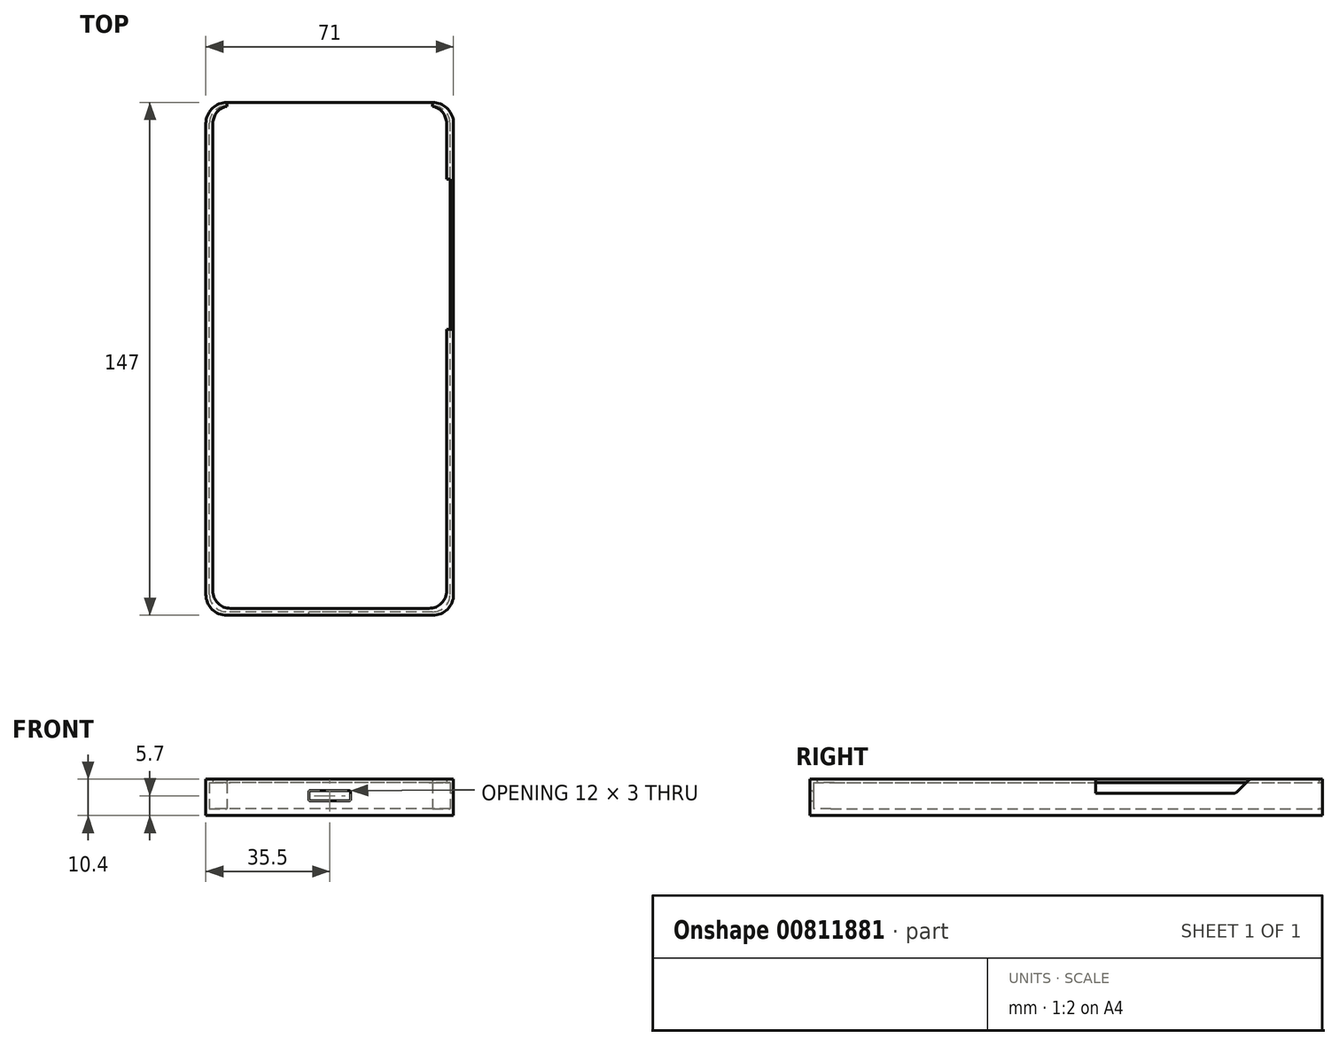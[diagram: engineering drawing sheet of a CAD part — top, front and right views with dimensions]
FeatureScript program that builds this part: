
annotation { "Feature Type Name" : "Feature", "Feature Type Description" : "" }
export const myFeature = defineFeature(function(context is Context, id is Id, definition is map)
    precondition{}
    {
        {
            var Q0;
            Q0=qCreatedBy(makeId("Top.planeOp"),FACE);
            var sketch = newSketch(context, id + "F0", { "sketchPlane" : qUnion([Q0])});
            skLineSegment(sketch, "E0.bottom", {"start": v(29.5, -72.5) * mm, "end": v(-29.5, -72.5) * mm});
            skLineSegment(sketch, "E0.top", {"start": v(29.5, 72.5) * mm, "end": v(-29.5, 72.5) * mm});
            skLineSegment(sketch, "E0.left", {"start": v(34.5, -67.5) * mm, "end": v(34.5, 67.5) * mm});
            skLineSegment(sketch, "E0.right", {"start": v(-34.5, -67.5) * mm, "end": v(-34.5, 67.5) * mm});
            skPoint(sketch, "E0.middle", {"position": v(0, 0) * mm});
            skLineSegment(sketch, "E1.bottom", {"start": v(29.5, -73.5) * mm, "end": v(-29.5, -73.5) * mm});
            skLineSegment(sketch, "E1.top", {"start": v(29.5, 73.5) * mm, "end": v(-29.5, 73.5) * mm});
            skLineSegment(sketch, "E1.left", {"start": v(35.5, -67.5) * mm, "end": v(35.5, 67.5) * mm});
            skLineSegment(sketch, "E1.right", {"start": v(-35.5, -67.5) * mm, "end": v(-35.5, 67.5) * mm});
            skPoint(sketch, "E2.visualSharp", {"position": v(-34.5, 72.5) * mm});
            skArc(sketch, "E2.filletArc", {"start": v(-29.5, 72.5) * mm, "mid": v(-33.04, 71.04) * mm, "end": v(-34.5, 67.5) * mm});
            skPoint(sketch, "E3.visualSharp", {"position": v(-34.5, -72.5) * mm});
            skArc(sketch, "E3.filletArc", {"start": v(-34.5, -67.5) * mm, "mid": v(-33.04, -71.04) * mm, "end": v(-29.5, -72.5) * mm});
            skPoint(sketch, "E4.visualSharp", {"position": v(34.5, -72.5) * mm});
            skArc(sketch, "E4.filletArc", {"start": v(29.5, -72.5) * mm, "mid": v(33.04, -71.04) * mm, "end": v(34.5, -67.5) * mm});
            skPoint(sketch, "E5.visualSharp", {"position": v(34.5, 72.5) * mm});
            skArc(sketch, "E5.filletArc", {"start": v(34.5, 67.5) * mm, "mid": v(33.04, 71.04) * mm, "end": v(29.5, 72.5) * mm});
            skPoint(sketch, "E6.visualSharp", {"position": v(-35.5, 73.5) * mm});
            skArc(sketch, "E6.filletArc", {"start": v(-29.5, 73.5) * mm, "mid": v(-33.74, 71.74) * mm, "end": v(-35.5, 67.5) * mm});
            skPoint(sketch, "E7.visualSharp", {"position": v(-35.5, -73.5) * mm});
            skArc(sketch, "E7.filletArc", {"start": v(-35.5, -67.5) * mm, "mid": v(-33.74, -71.74) * mm, "end": v(-29.5, -73.5) * mm});
            skPoint(sketch, "E8.visualSharp", {"position": v(35.5, -73.5) * mm});
            skArc(sketch, "E8.filletArc", {"start": v(29.5, -73.5) * mm, "mid": v(33.74, -71.74) * mm, "end": v(35.5, -67.5) * mm});
            skPoint(sketch, "E9.visualSharp", {"position": v(35.5, 73.5) * mm});
            skArc(sketch, "E9.filletArc", {"start": v(35.5, 67.5) * mm, "mid": v(33.74, 71.74) * mm, "end": v(29.5, 73.5) * mm});
            skSolve(sketch);
        }
        {
            var Q0;
            Q0=makeQuery(id+"F0.imprint","IMPRINT",FACE,{"disambiguationData":[TD([[makeQuery(id+"F0.imprint","IMPRINT",EDGE,{"derivedFrom":sQuery(id+"F0.wireOp",EDGE,"E0.bottom")}),-1.0]])]});
            extrude(context, id + "F1", {"entities" : qUnion([Q0]), "depth" : 1 * mm});
        }
        {
            var Q0;
            Q0=makeQuery(id+"F0.imprint","IMPRINT",FACE,{"disambiguationData":[TD([[makeQuery(id+"F0.imprint","IMPRINT",EDGE,{"derivedFrom":sQuery(id+"F0.wireOp",EDGE,"E0.bottom")}),1.0]])]});
            extrude(context, id + "F2", {"entities" : qUnion([Q0]), "operationType" : NewBodyOperationType.ADD, "depth" : (1 + 7.4) * mm});
        }
        {
            var Q0;
            Q0=makeQuery(id+"F2.opExtrude","CAP_FACE",FACE,{"disambiguationData":[OSD([sQuery(id+"F0.wireOp",EDGE,"E0.bottom"),sQuery(id+"F0.wireOp",EDGE,"E0.top"),sQuery(id+"F0.wireOp",EDGE,"E0.left"),sQuery(id+"F0.wireOp",EDGE,"E0.right"),sQuery(id+"F0.wireOp",EDGE,"E1.bottom"),sQuery(id+"F0.wireOp",EDGE,"E1.top"),sQuery(id+"F0.wireOp",EDGE,"E1.left"),sQuery(id+"F0.wireOp",EDGE,"E1.right"),sQuery(id+"F0.wireOp",EDGE,"E2.filletArc"),sQuery(id+"F0.wireOp",EDGE,"E3.filletArc"),sQuery(id+"F0.wireOp",EDGE,"E4.filletArc"),sQuery(id+"F0.wireOp",EDGE,"E5.filletArc"),sQuery(id+"F0.wireOp",EDGE,"E6.filletArc"),sQuery(id+"F0.wireOp",EDGE,"E7.filletArc"),sQuery(id+"F0.wireOp",EDGE,"E8.filletArc"),sQuery(id+"F0.wireOp",EDGE,"E9.filletArc")])],"isStart":false});
            var sketch = newSketch(context, id + "F3", { "sketchPlane" : qUnion([Q0])});
            skLineSegment(sketch, "E10.bottom", {"start": v(28.5, -71.5) * mm, "end": v(-28.5, -71.5) * mm});
            skLineSegment(sketch, "E10.top", {"start": v(28.5, 72.5) * mm, "end": v(-28.5, 72.5) * mm});
            skLineSegment(sketch, "E10.left", {"start": v(33.5, -66.5) * mm, "end": v(33.5, 67.5) * mm});
            skLineSegment(sketch, "E10.right", {"start": v(-33.5, -66.5) * mm, "end": v(-33.5, 67.5) * mm});
            skPoint(sketch, "E10.middle", {"position": v(0, 0.5) * mm});
            skPoint(sketch, "E11.visualSharp", {"position": v(-33.5, -71.5) * mm});
            skArc(sketch, "E11.filletArc", {"start": v(-33.5, -66.5) * mm, "mid": v(-32.04, -70.04) * mm, "end": v(-28.5, -71.5) * mm});
            skPoint(sketch, "E12.visualSharp", {"position": v(33.5, -71.5) * mm});
            skArc(sketch, "E12.filletArc", {"start": v(28.5, -71.5) * mm, "mid": v(32.04, -70.04) * mm, "end": v(33.5, -66.5) * mm});
            skPoint(sketch, "E13.visualSharp", {"position": v(33.5, 72.5) * mm});
            skArc(sketch, "E13.filletArc", {"start": v(33.5, 67.5) * mm, "mid": v(32.04, 71.04) * mm, "end": v(28.5, 72.5) * mm});
            skPoint(sketch, "E14.visualSharp", {"position": v(-33.5, 72.5) * mm});
            skArc(sketch, "E14.filletArc", {"start": v(-28.5, 72.5) * mm, "mid": v(-32.04, 71.04) * mm, "end": v(-33.5, 67.5) * mm});
            skSolve(sketch);
        }
        {
            var Q0;
            Q0=makeQuery(id+"F3.imprint","IMPRINT",FACE,{"disambiguationData":[TD([[makeQuery(id+"F3.imprint","IMPRINT",EDGE,{"derivedFrom":sQuery(id+"F3.wireOp",EDGE,"E10.bottom")}),1.0]])]});
            var Q1;
            Q1=makeQuery(id+"F3.imprint","IMPRINT",FACE,{"disambiguationData":[TD([[makeQuery(id+"F3.imprint","IMPRINT",EDGE,{"derivedFrom":makeQuery(id+"F2.opExtrude","CAP_EDGE",EDGE,{"disambiguationData":[OSD([sQuery(id+"F0.wireOp",EDGE,"E0.bottom")])],"isStart":false})}),1.0]])]});
            extrude(context, id + "F4", {"entities" : qUnion([Q0, Q1]), "operationType" : NewBodyOperationType.ADD, "depth" : 1 * mm});
        }
        {
            var Q0;
            Q0=makeQuery(id+"F4.boolean.opBoolean","MERGE",FACE,{"derivedFrom":[makeQuery(id+"F2.opExtrude","SWEPT_FACE",FACE,{"disambiguationData":[OSD([sQuery(id+"F0.wireOp",EDGE,"E0.top")])]}),makeQuery(id+"F4.opExtrude","SWEPT_FACE",FACE,{"disambiguationData":[OSD([sQuery(id+"F3.wireOp",EDGE,"E10.top")])]})]});
            extrude(context, id + "F5", {"entities" : qUnion([Q0]), "operationType" : NewBodyOperationType.REMOVE, "endBound" : BoundingType.THROUGH_ALL, "oppositeDirection" : true, "depth" : 25 * mm});
        }
        {
            var Q0;
            {var subQ2=sQuery(id+"F0.wireOp",EDGE,"E0.top");var subQ3=sQuery(id+"F3.wireOp",EDGE,"E14.filletArc");var subQ9=sQuery(id+"F3.wireOp",EDGE,"E10.top");var subQ16=sQuery(id+"F0.wireOp",EDGE,"E1.top");Q0=makeQuery(id+"F5.boolean.opBoolean","SPLIT",FACE,{"disambiguationData":[TD([makeQuery(id+"F5.opExtrude","SWEPT_FACE",FACE,{"disambiguationData":[OSD([subQ2,subQ9,subQ3])]})])],"derivedFrom":makeQuery(id+"F4.boolean.opBoolean","MERGE",FACE,{"derivedFrom":[makeQuery(id+"F2.opExtrude","SWEPT_FACE",FACE,{"disambiguationData":[OSD([subQ16])]}),makeQuery(id+"F4.opExtrude","SWEPT_FACE",FACE,{"disambiguationData":[OSD([subQ16])]})]})});}
            var Q1;
            {var subQ2=sQuery(id+"F3.wireOp",EDGE,"E13.filletArc");var subQ7=sQuery(id+"F3.wireOp",EDGE,"E10.top");var subQ14=sQuery(id+"F0.wireOp",EDGE,"E1.top");var subQ17=sQuery(id+"F0.wireOp",EDGE,"E0.top");Q1=makeQuery(id+"F5.boolean.opBoolean","SPLIT",FACE,{"disambiguationData":[TD([makeQuery(id+"F5.opExtrude","SWEPT_FACE",FACE,{"disambiguationData":[OSD([subQ17,subQ7,subQ2])]})])],"derivedFrom":makeQuery(id+"F4.boolean.opBoolean","MERGE",FACE,{"derivedFrom":[makeQuery(id+"F2.opExtrude","SWEPT_FACE",FACE,{"disambiguationData":[OSD([subQ14])]}),makeQuery(id+"F4.opExtrude","SWEPT_FACE",FACE,{"disambiguationData":[OSD([subQ14])]})]})});}
            extrude(context, id + "F6", {"entities" : qUnion([Q0, Q1]), "operationType" : NewBodyOperationType.REMOVE, "endBound" : BoundingType.UP_TO_NEXT, "oppositeDirection" : true, "depth" : 25 * mm});
        }
        {
            var Q0;
            {var subQ0=sQuery(id+"F0.wireOp",EDGE,"E9.filletArc");var subQ1=sQuery(id+"F0.wireOp",EDGE,"E1.top");var subQ2=makeQuery(id+"F2.opExtrude","SWEPT_FACE",FACE,{"disambiguationData":[OSD([subQ0])]});var subQ3=sQuery(id+"F0.wireOp",EDGE,"E5.filletArc");var subQ4=sQuery(id+"F0.wireOp",EDGE,"E0.top");var subQ5=makeQuery(id+"F5.opExtrude","SWEPT_FACE",FACE,{"disambiguationData":[OSD([subQ4,subQ3])]});var subQ6=makeQuery(id+"F4.opExtrude","SWEPT_FACE",FACE,{"disambiguationData":[OSD([subQ0])]});var subQ7=makeQuery(id+"F4.boolean.opBoolean","MERGE",EDGE,{"derivedFrom":[makeQuery(id+"F2.opExtrude","SWEPT_EDGE",EDGE,{"disambiguationData":[OSD([subQ1,subQ0])]}),makeQuery(id+"F4.opExtrude","SWEPT_EDGE",EDGE,{"disambiguationData":[OSD([subQ1,subQ0])]})]});var subQ22=makeQuery(id+"F2.opExtrude","SWEPT_FACE",FACE,{"disambiguationData":[OSD([subQ1])]});var subQ24=makeQuery(id+"F4.opExtrude","SWEPT_FACE",FACE,{"disambiguationData":[OSD([subQ1])]});var subQ27=makeQuery(id+"F2.opExtrude","CAP_EDGE",EDGE,{"disambiguationData":[OSD([subQ4])],"isStart":false});Q0=makeQuery(id+"F6.boolean.opBoolean","MERGE",EDGE,{"derivedFrom":[makeQuery(id+"F5.boolean.opBoolean","SPLIT",EDGE,{"disambiguationData":[topologyDisambiguationEdgeConnected([subQ22,subQ2,subQ24,subQ6]),TD([makeQuery(id+"F5.opExtrude","SWEPT_FACE",FACE,{"disambiguationData":[OSD([subQ4]),TDD([makeQuery(id+"F4.boolean.opBoolean","SPLIT",EDGE,{"disambiguationData":[TD([makeQuery(id+"F2.opExtrude","SWEPT_FACE",FACE,{"disambiguationData":[OSD([subQ3])]})])],"derivedFrom":subQ27})])]})])],"derivedFrom":subQ7}),makeQuery(id+"F5.boolean.opBoolean","SPLIT",EDGE,{"disambiguationData":[topologyDisambiguationEdgeConnected([subQ2,subQ6,subQ5])],"derivedFrom":subQ7})],"fromTools":[makeQuery(id+"F6.opExtrude","CAP_EDGE",EDGE,{"disambiguationData":[OSD([subQ1,subQ0])],"isStart":true})]});}
            var Q1;
            {var subQ0=sQuery(id+"F0.wireOp",EDGE,"E6.filletArc");var subQ1=sQuery(id+"F0.wireOp",EDGE,"E1.top");var subQ2=makeQuery(id+"F2.opExtrude","SWEPT_FACE",FACE,{"disambiguationData":[OSD([subQ0])]});var subQ3=makeQuery(id+"F4.opExtrude","SWEPT_FACE",FACE,{"disambiguationData":[OSD([subQ0])]});var subQ4=sQuery(id+"F0.wireOp",EDGE,"E2.filletArc");var subQ5=sQuery(id+"F0.wireOp",EDGE,"E0.top");var subQ6=makeQuery(id+"F5.opExtrude","SWEPT_FACE",FACE,{"disambiguationData":[OSD([subQ5,subQ4])]});var subQ7=makeQuery(id+"F4.boolean.opBoolean","MERGE",EDGE,{"derivedFrom":[makeQuery(id+"F2.opExtrude","SWEPT_EDGE",EDGE,{"disambiguationData":[OSD([subQ1,subQ0])]}),makeQuery(id+"F4.opExtrude","SWEPT_EDGE",EDGE,{"disambiguationData":[OSD([subQ1,subQ0])]})]});var subQ22=makeQuery(id+"F2.opExtrude","SWEPT_FACE",FACE,{"disambiguationData":[OSD([subQ1])]});var subQ24=makeQuery(id+"F4.opExtrude","SWEPT_FACE",FACE,{"disambiguationData":[OSD([subQ1])]});var subQ27=makeQuery(id+"F2.opExtrude","CAP_EDGE",EDGE,{"disambiguationData":[OSD([subQ5])],"isStart":false});Q1=makeQuery(id+"F6.boolean.opBoolean","MERGE",EDGE,{"derivedFrom":[makeQuery(id+"F5.boolean.opBoolean","SPLIT",EDGE,{"disambiguationData":[topologyDisambiguationEdgeConnected([subQ22,subQ2,subQ24,subQ3]),TD([makeQuery(id+"F5.opExtrude","SWEPT_FACE",FACE,{"disambiguationData":[OSD([subQ5]),TDD([makeQuery(id+"F4.boolean.opBoolean","SPLIT",EDGE,{"disambiguationData":[TD([makeQuery(id+"F2.opExtrude","SWEPT_FACE",FACE,{"disambiguationData":[OSD([sQuery(id+"F0.wireOp",EDGE,"E5.filletArc")])]})])],"derivedFrom":subQ27})])]})])],"derivedFrom":subQ7}),makeQuery(id+"F5.boolean.opBoolean","SPLIT",EDGE,{"disambiguationData":[topologyDisambiguationEdgeConnected([subQ2,subQ3,subQ6])],"derivedFrom":subQ7})],"fromTools":[makeQuery(id+"F6.opExtrude","CAP_EDGE",EDGE,{"disambiguationData":[OSD([subQ1,subQ0])],"isStart":true})]});}
            var Q2;
            {var subQ0=sQuery(id+"F0.wireOp",EDGE,"E2.filletArc");var subQ1=sQuery(id+"F0.wireOp",EDGE,"E0.top");Q2=makeQuery(id+"F5.boolean.opBoolean","MERGE",EDGE,{"derivedFrom":[makeQuery(id+"F2.opExtrude","SWEPT_EDGE",EDGE,{"disambiguationData":[OSD([subQ1,subQ0])]}),makeQuery(id+"F5.opExtrude","CAP_EDGE",EDGE,{"disambiguationData":[OSD([subQ1,subQ0])],"isStart":true})]});}
            var Q3;
            {var subQ0=sQuery(id+"F0.wireOp",EDGE,"E5.filletArc");var subQ1=sQuery(id+"F0.wireOp",EDGE,"E0.top");Q3=makeQuery(id+"F5.boolean.opBoolean","MERGE",EDGE,{"derivedFrom":[makeQuery(id+"F2.opExtrude","SWEPT_EDGE",EDGE,{"disambiguationData":[OSD([subQ1,subQ0])]}),makeQuery(id+"F5.opExtrude","CAP_EDGE",EDGE,{"disambiguationData":[OSD([subQ1,subQ0])],"isStart":true})]});}
            fillet(context, id + "F7", {"entities" : qUnion([Q0, Q1, Q2, Q3]), "radius" : 0.5 * mm, "tangentPropagation" : true, "allowEdgeOverflow" : false});
        }
        {
            var Q0;
            Q0=makeQuery(id+"F2.opExtrude","SWEPT_FACE",FACE,{"disambiguationData":[OSD([sQuery(id+"F0.wireOp",EDGE,"E0.bottom")])]});
            var sketch = newSketch(context, id + "F8", { "sketchPlane" : qUnion([Q0])});
            skLineSegment(sketch, "E15", {"start": v(0, 1) * mm, "end": v(0, 8.4) * mm, "construction": true});
            skLineSegment(sketch, "E16.bottom", {"start": v(-6, 6.2) * mm, "end": v(6, 6.2) * mm});
            skLineSegment(sketch, "E16.top", {"start": v(-6, 3.2) * mm, "end": v(6, 3.2) * mm});
            skLineSegment(sketch, "E16.left", {"start": v(-6, 6.2) * mm, "end": v(-6, 3.2) * mm});
            skLineSegment(sketch, "E16.right", {"start": v(6, 6.2) * mm, "end": v(6, 3.2) * mm});
            skPoint(sketch, "E16.middle", {"position": v(0, 4.7) * mm});
            skSolve(sketch);
        }
        {
            var Q0;
            Q0=makeQuery(id+"F8.imprint","IMPRINT",FACE,{"disambiguationData":[TD([[makeQuery(id+"F8.imprint","IMPRINT",EDGE,{"derivedFrom":sQuery(id+"F8.wireOp",EDGE,"E16.bottom")}),-1.0]])]});
            extrude(context, id + "F9", {"entities" : qUnion([Q0]), "operationType" : NewBodyOperationType.REMOVE, "endBound" : BoundingType.UP_TO_NEXT, "oppositeDirection" : true, "depth" : 25 * mm});
        }
        {
            var Q0;
            Q0=makeQuery(id+"F9.boolean.opBoolean","COPY",EDGE,{"derivedFrom":makeQuery(id+"F9.opExtrude","SWEPT_EDGE",EDGE,{"disambiguationData":[OSD([sQuery(id+"F8.wireOp",EDGE,"E16.top"),sQuery(id+"F8.wireOp",EDGE,"E16.right")])]})});
            var Q1;
            Q1=makeQuery(id+"F9.boolean.opBoolean","COPY",EDGE,{"derivedFrom":makeQuery(id+"F9.opExtrude","SWEPT_EDGE",EDGE,{"disambiguationData":[OSD([sQuery(id+"F8.wireOp",EDGE,"E16.top"),sQuery(id+"F8.wireOp",EDGE,"E16.left")])]})});
            var Q2;
            Q2=makeQuery(id+"F9.boolean.opBoolean","COPY",EDGE,{"derivedFrom":makeQuery(id+"F9.opExtrude","SWEPT_EDGE",EDGE,{"disambiguationData":[OSD([sQuery(id+"F8.wireOp",EDGE,"E16.bottom"),sQuery(id+"F8.wireOp",EDGE,"E16.right")])]})});
            var Q3;
            Q3=makeQuery(id+"F9.boolean.opBoolean","COPY",EDGE,{"derivedFrom":makeQuery(id+"F9.opExtrude","SWEPT_EDGE",EDGE,{"disambiguationData":[OSD([sQuery(id+"F8.wireOp",EDGE,"E16.bottom"),sQuery(id+"F8.wireOp",EDGE,"E16.left")])]})});
            fillet(context, id + "F10", {"entities" : qUnion([Q0, Q1, Q2, Q3]), "radius" : 0.5 * mm, "tangentPropagation" : true, "allowEdgeOverflow" : false});
        }
        {
            var Q0;
            {var subQ0=sQuery(id+"F0.wireOp",EDGE,"E1.left");Q0=makeQuery(id+"F4.boolean.opBoolean","MERGE",FACE,{"derivedFrom":[makeQuery(id+"F2.opExtrude","SWEPT_FACE",FACE,{"disambiguationData":[OSD([subQ0])]}),makeQuery(id+"F4.opExtrude","SWEPT_FACE",FACE,{"disambiguationData":[OSD([subQ0])]})]});}
            var sketch = newSketch(context, id + "F11", { "sketchPlane" : qUnion([Q0])});
            skLineSegment(sketch, "E17.bottom", {"start": v(48.48, 9.4) * mm, "end": v(8.48, 9.4) * mm});
            skLineSegment(sketch, "E17.top", {"start": v(48.48, 5.4) * mm, "end": v(8.48, 5.4) * mm});
            skLineSegment(sketch, "E17.left", {"start": v(48.48, 9.4) * mm, "end": v(48.48, 5.4) * mm});
            skLineSegment(sketch, "E17.right", {"start": v(8.48, 9.4) * mm, "end": v(8.48, 5.4) * mm});
            skSolve(sketch);
        }
        {
            var Q0;
            Q0=qSketchRegion(id+"F11",true);
            extrude(context, id + "F12", {"entities" : qUnion([Q0]), "operationType" : NewBodyOperationType.REMOVE, "endBound" : BoundingType.UP_TO_NEXT, "oppositeDirection" : true, "depth" : 25 * mm});
        }
        {
            var Q0;
            Q0=makeQuery(id+"F12.boolean.opBoolean","COPY",EDGE,{"derivedFrom":makeQuery(id+"F12.opExtrude","SWEPT_EDGE",EDGE,{"disambiguationData":[OSD([sQuery(id+"F0.wireOp",EDGE,"E1.left"),sQuery(id+"F11.wireOp",EDGE,"E17.bottom"),sQuery(id+"F11.wireOp",EDGE,"E17.left")])]})});
            var Q1;
            Q1=makeQuery(id+"F12.boolean.opBoolean","COPY",EDGE,{"derivedFrom":makeQuery(id+"F12.opExtrude","SWEPT_EDGE",EDGE,{"disambiguationData":[OSD([sQuery(id+"F0.wireOp",EDGE,"E1.left"),sQuery(id+"F11.wireOp",EDGE,"E17.bottom"),sQuery(id+"F11.wireOp",EDGE,"E17.right")])]})});
            chamfer(context, id + "F13", {"entities" : qUnion([Q0, Q1]), "width" : 4 * mm, "tangentPropagation" : true});
        }
        {
            var Q0;
            Q0=makeQuery(id+"F13.opChamfer","BLEND_EDGE",EDGE,{"blendedFrom":[makeQuery(id+"F12.boolean.opBoolean","COPY",EDGE,{"derivedFrom":makeQuery(id+"F12.opExtrude","SWEPT_EDGE",EDGE,{"disambiguationData":[OSD([sQuery(id+"F0.wireOp",EDGE,"E1.left"),sQuery(id+"F11.wireOp",EDGE,"E17.bottom"),sQuery(id+"F11.wireOp",EDGE,"E17.left")])]})}),makeQuery(id+"F12.boolean.opBoolean","COPY",FACE,{"derivedFrom":makeQuery(id+"F12.opExtrude","SWEPT_FACE",FACE,{"disambiguationData":[OSD([sQuery(id+"F11.wireOp",EDGE,"E17.top")])]})})],"blendedInto":[makeQuery(id+"F12.boolean.opBoolean","COPY",FACE,{"derivedFrom":makeQuery(id+"F12.opExtrude","SWEPT_FACE",FACE,{"disambiguationData":[OSD([sQuery(id+"F11.wireOp",EDGE,"E17.top")])]})})]});
            var Q1;
            Q1=makeQuery(id+"F13.opChamfer","BLEND_EDGE",EDGE,{"blendedFrom":[makeQuery(id+"F12.boolean.opBoolean","COPY",EDGE,{"derivedFrom":makeQuery(id+"F12.opExtrude","SWEPT_EDGE",EDGE,{"disambiguationData":[OSD([sQuery(id+"F0.wireOp",EDGE,"E1.left"),sQuery(id+"F11.wireOp",EDGE,"E17.bottom"),sQuery(id+"F11.wireOp",EDGE,"E17.right")])]})}),makeQuery(id+"F12.boolean.opBoolean","COPY",FACE,{"derivedFrom":makeQuery(id+"F12.opExtrude","SWEPT_FACE",FACE,{"disambiguationData":[OSD([sQuery(id+"F11.wireOp",EDGE,"E17.top")])]})})],"blendedInto":[makeQuery(id+"F12.boolean.opBoolean","COPY",FACE,{"derivedFrom":makeQuery(id+"F12.opExtrude","SWEPT_FACE",FACE,{"disambiguationData":[OSD([sQuery(id+"F11.wireOp",EDGE,"E17.top")])]})})]});
            fillet(context, id + "F14", {"entities" : qUnion([Q0, Q1]), "radius" : 1 * mm, "tangentPropagation" : true, "allowEdgeOverflow" : false});
        }
        {
            var Q0;
            {var subQ0=sQuery(id+"F3.wireOp",EDGE,"E13.filletArc");var subQ1=sQuery(id+"F0.wireOp",EDGE,"E9.filletArc");var subQ2=sQuery(id+"F0.wireOp",EDGE,"E1.left");var subQ3=sQuery(id+"F3.wireOp",EDGE,"E10.left");var subQ4=sQuery(id+"F11.wireOp",EDGE,"E17.left");Q0=makeQuery(id+"F13.opChamfer","BLEND_EDGE",EDGE,{"blendedFrom":[makeQuery(id+"F12.boolean.opBoolean","COPY",EDGE,{"derivedFrom":makeQuery(id+"F12.opExtrude","SWEPT_EDGE",EDGE,{"disambiguationData":[OSD([subQ2,sQuery(id+"F11.wireOp",EDGE,"E17.bottom"),subQ4])]})}),makeQuery(id+"F12.boolean.opBoolean","SPLIT",FACE,{"disambiguationData":[TD([makeQuery(id+"F2.opExtrude","SWEPT_FACE",FACE,{"disambiguationData":[OSD([subQ1])]})])],"derivedFrom":makeQuery(id+"F4.opExtrude","CAP_FACE",FACE,{"disambiguationData":[OSD([sQuery(id+"F0.wireOp",EDGE,"E1.bottom"),sQuery(id+"F0.wireOp",EDGE,"E1.top"),subQ2,sQuery(id+"F0.wireOp",EDGE,"E1.right"),sQuery(id+"F0.wireOp",EDGE,"E6.filletArc"),sQuery(id+"F0.wireOp",EDGE,"E7.filletArc"),sQuery(id+"F0.wireOp",EDGE,"E8.filletArc"),subQ1,sQuery(id+"F3.wireOp",EDGE,"E10.bottom"),sQuery(id+"F3.wireOp",EDGE,"E10.top"),subQ3,sQuery(id+"F3.wireOp",EDGE,"E10.right"),sQuery(id+"F3.wireOp",EDGE,"E11.filletArc"),sQuery(id+"F3.wireOp",EDGE,"E12.filletArc"),subQ0,sQuery(id+"F3.wireOp",EDGE,"E14.filletArc")])],"isStart":false})})],"blendedInto":[makeQuery(id+"F12.boolean.opBoolean","SPLIT",FACE,{"disambiguationData":[TD([makeQuery(id+"F2.opExtrude","SWEPT_FACE",FACE,{"disambiguationData":[OSD([subQ1])]})])],"derivedFrom":makeQuery(id+"F4.opExtrude","CAP_FACE",FACE,{"disambiguationData":[OSD([sQuery(id+"F0.wireOp",EDGE,"E1.bottom"),sQuery(id+"F0.wireOp",EDGE,"E1.top"),subQ2,sQuery(id+"F0.wireOp",EDGE,"E1.right"),sQuery(id+"F0.wireOp",EDGE,"E6.filletArc"),sQuery(id+"F0.wireOp",EDGE,"E7.filletArc"),sQuery(id+"F0.wireOp",EDGE,"E8.filletArc"),subQ1,sQuery(id+"F3.wireOp",EDGE,"E10.bottom"),sQuery(id+"F3.wireOp",EDGE,"E10.top"),subQ3,sQuery(id+"F3.wireOp",EDGE,"E10.right"),sQuery(id+"F3.wireOp",EDGE,"E11.filletArc"),sQuery(id+"F3.wireOp",EDGE,"E12.filletArc"),subQ0,sQuery(id+"F3.wireOp",EDGE,"E14.filletArc")])],"isStart":false})})]});}
            var Q1;
            {var subQ0=sQuery(id+"F3.wireOp",EDGE,"E11.filletArc");var subQ1=sQuery(id+"F3.wireOp",EDGE,"E10.right");var subQ2=sQuery(id+"F3.wireOp",EDGE,"E10.bottom");var subQ3=sQuery(id+"F0.wireOp",EDGE,"E8.filletArc");var subQ4=sQuery(id+"F0.wireOp",EDGE,"E7.filletArc");var subQ5=sQuery(id+"F0.wireOp",EDGE,"E1.bottom");var subQ6=sQuery(id+"F0.wireOp",EDGE,"E1.left");var subQ7=sQuery(id+"F3.wireOp",EDGE,"E10.left");var subQ8=sQuery(id+"F0.wireOp",EDGE,"E1.right");var subQ9=sQuery(id+"F0.wireOp",EDGE,"E6.filletArc");var subQ10=sQuery(id+"F3.wireOp",EDGE,"E12.filletArc");var subQ13=sQuery(id+"F3.wireOp",EDGE,"E14.filletArc");var subQ14=sQuery(id+"F11.wireOp",EDGE,"E17.right");Q1=makeQuery(id+"F13.opChamfer","BLEND_EDGE",EDGE,{"blendedFrom":[makeQuery(id+"F12.boolean.opBoolean","COPY",EDGE,{"derivedFrom":makeQuery(id+"F12.opExtrude","SWEPT_EDGE",EDGE,{"disambiguationData":[OSD([subQ6,sQuery(id+"F11.wireOp",EDGE,"E17.bottom"),subQ14])]})}),makeQuery(id+"F12.boolean.opBoolean","SPLIT",FACE,{"disambiguationData":[TD([makeQuery(id+"F2.opExtrude","SWEPT_FACE",FACE,{"disambiguationData":[OSD([subQ5])]})])],"derivedFrom":makeQuery(id+"F4.opExtrude","CAP_FACE",FACE,{"disambiguationData":[OSD([subQ5,sQuery(id+"F0.wireOp",EDGE,"E1.top"),subQ6,subQ8,subQ9,subQ4,subQ3,sQuery(id+"F0.wireOp",EDGE,"E9.filletArc"),subQ2,sQuery(id+"F3.wireOp",EDGE,"E10.top"),subQ7,subQ1,subQ0,subQ10,sQuery(id+"F3.wireOp",EDGE,"E13.filletArc"),subQ13])],"isStart":false})})],"blendedInto":[makeQuery(id+"F12.boolean.opBoolean","SPLIT",FACE,{"disambiguationData":[TD([makeQuery(id+"F2.opExtrude","SWEPT_FACE",FACE,{"disambiguationData":[OSD([subQ5])]})])],"derivedFrom":makeQuery(id+"F4.opExtrude","CAP_FACE",FACE,{"disambiguationData":[OSD([subQ5,sQuery(id+"F0.wireOp",EDGE,"E1.top"),subQ6,subQ8,subQ9,subQ4,subQ3,sQuery(id+"F0.wireOp",EDGE,"E9.filletArc"),subQ2,sQuery(id+"F3.wireOp",EDGE,"E10.top"),subQ7,subQ1,subQ0,subQ10,sQuery(id+"F3.wireOp",EDGE,"E13.filletArc"),subQ13])],"isStart":false})})]});}
            fillet(context, id + "F15", {"entities" : qUnion([Q0, Q1]), "radius" : 1 * mm, "tangentPropagation" : true, "allowEdgeOverflow" : false});
        }
        {
            var Q0;
            {var subQ0=sQuery(id+"F0.wireOp",EDGE,"E5.filletArc");var subQ1=sQuery(id+"F0.wireOp",EDGE,"E4.filletArc");var subQ2=sQuery(id+"F0.wireOp",EDGE,"E3.filletArc");var subQ3=sQuery(id+"F0.wireOp",EDGE,"E2.filletArc");var subQ4=sQuery(id+"F0.wireOp",EDGE,"E0.right");var subQ5=sQuery(id+"F0.wireOp",EDGE,"E0.left");var subQ6=sQuery(id+"F0.wireOp",EDGE,"E0.top");var subQ7=sQuery(id+"F0.wireOp",EDGE,"E0.bottom");Q0=makeQuery(id+"F2.boolean.opBoolean","MERGE",FACE,{"derivedFrom":[makeQuery(id+"F1.opExtrude","CAP_FACE",FACE,{"disambiguationData":[OSD([subQ7,subQ6,subQ5,subQ4,subQ3,subQ2,subQ1,subQ0])],"isStart":true}),makeQuery(id+"F2.opExtrude","CAP_FACE",FACE,{"disambiguationData":[OSD([subQ7,subQ6,subQ5,subQ4,sQuery(id+"F0.wireOp",EDGE,"E1.bottom"),sQuery(id+"F0.wireOp",EDGE,"E1.top"),sQuery(id+"F0.wireOp",EDGE,"E1.left"),sQuery(id+"F0.wireOp",EDGE,"E1.right"),subQ3,subQ2,subQ1,subQ0,sQuery(id+"F0.wireOp",EDGE,"E6.filletArc"),sQuery(id+"F0.wireOp",EDGE,"E7.filletArc"),sQuery(id+"F0.wireOp",EDGE,"E8.filletArc"),sQuery(id+"F0.wireOp",EDGE,"E9.filletArc")])],"isStart":true})]});}
            extrude(context, id + "F16", {"entities" : qUnion([Q0]), "operationType" : NewBodyOperationType.ADD, "depth" : 1 * mm, "offsetDistance" : 25 * mm});
        }
    });
